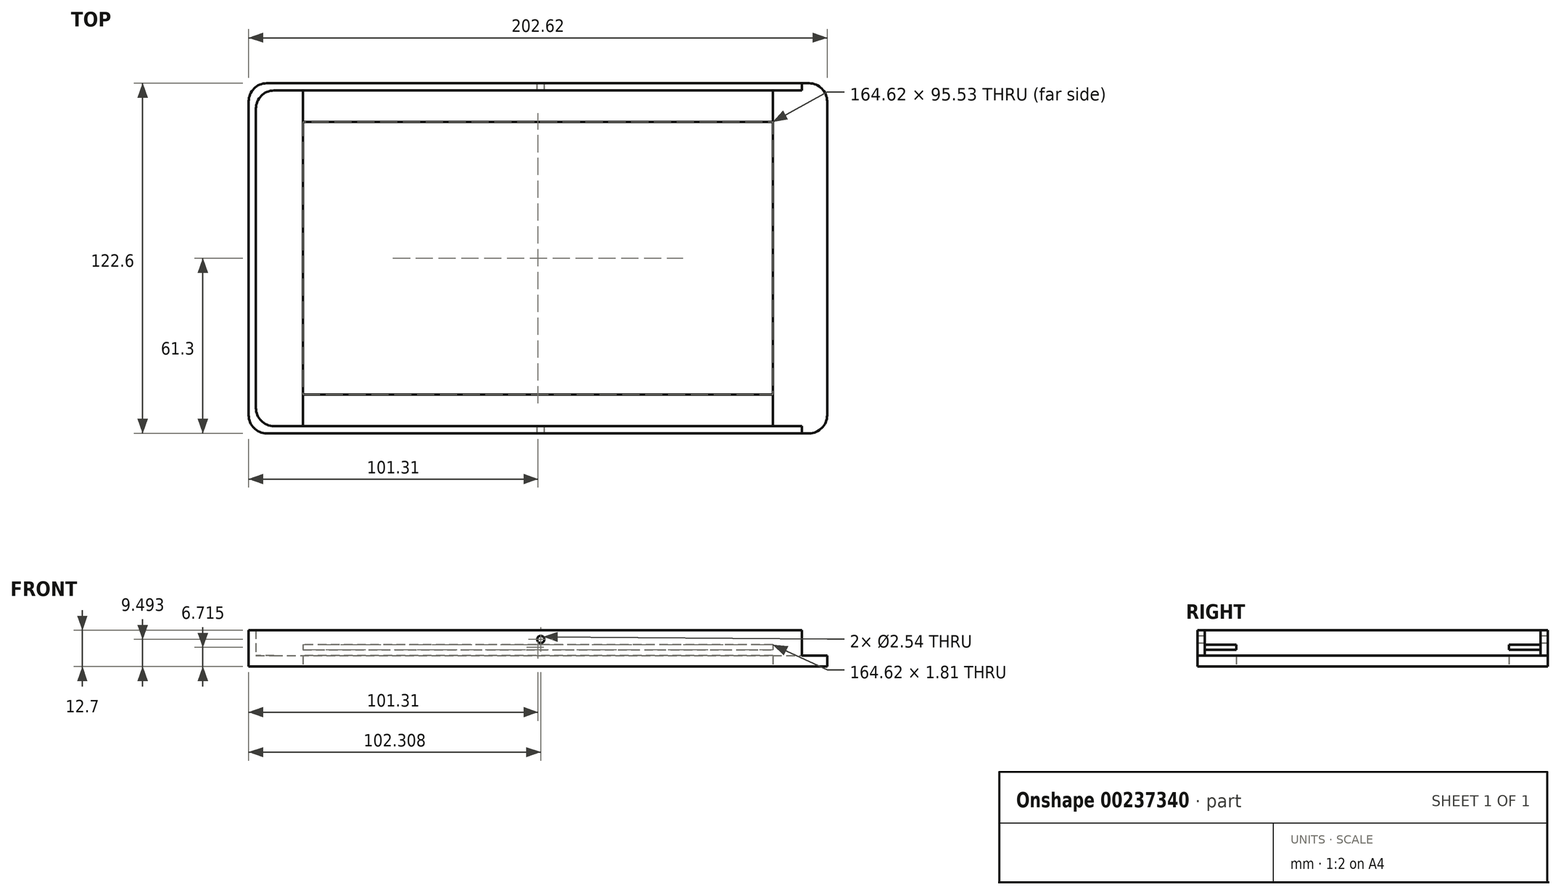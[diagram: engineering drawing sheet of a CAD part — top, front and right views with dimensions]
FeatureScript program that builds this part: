
annotation { "Feature Type Name" : "Feature", "Feature Type Description" : "" }
export const myFeature = defineFeature(function(context is Context, id is Id, definition is map)
    precondition{}
    {
        {
            var Q0;
            Q0=qCreatedBy(makeId("Top.planeOp"),FACE);
            var sketch = newSketch(context, id + "F0", { "sketchPlane" : qUnion([Q0])});
            skLineSegment(sketch, "E0.bottom", {"start": v(94.96, -61.3) * mm, "end": v(-94.96, -61.3) * mm});
            skLineSegment(sketch, "E0.top", {"start": v(94.96, 61.3) * mm, "end": v(-94.96, 61.3) * mm});
            skLineSegment(sketch, "E0.left", {"start": v(101.3, -54.95) * mm, "end": v(101.3, 54.95) * mm});
            skLineSegment(sketch, "E0.right", {"start": v(-101.3, -54.95) * mm, "end": v(-101.3, 54.95) * mm});
            skPoint(sketch, "E0.middle", {"position": v(0, 0) * mm});
            skPoint(sketch, "E1.visualSharp", {"position": v(101.3, -61.3) * mm});
            skArc(sketch, "E1.filletArc", {"start": v(94.96, -61.3) * mm, "mid": v(99.45, -59.44) * mm, "end": v(101.3, -54.95) * mm});
            skPoint(sketch, "E2.visualSharp", {"position": v(-101.3, -61.3) * mm});
            skArc(sketch, "E2.filletArc", {"start": v(-101.3, -54.95) * mm, "mid": v(-99.45, -59.44) * mm, "end": v(-94.96, -61.3) * mm});
            skPoint(sketch, "E3.visualSharp", {"position": v(-101.3, 61.3) * mm});
            skArc(sketch, "E3.filletArc", {"start": v(-94.96, 61.3) * mm, "mid": v(-99.45, 59.44) * mm, "end": v(-101.3, 54.95) * mm});
            skPoint(sketch, "E4.visualSharp", {"position": v(101.3, 61.3) * mm});
            skArc(sketch, "E4.filletArc", {"start": v(101.3, 54.95) * mm, "mid": v(99.45, 59.44) * mm, "end": v(94.96, 61.3) * mm});
            skLineSegment(sketch, "E5.0", {"start": v(-82.3, -54.95) * mm, "end": v(-82.3, 54.95) * mm});
            skLineSegment(sketch, "E6.0", {"start": v(82.3, -54.95) * mm, "end": v(-82.3, -54.95) * mm});
            skLineSegment(sketch, "E7.0", {"start": v(82.3, -54.95) * mm, "end": v(82.3, 54.95) * mm});
            skLineSegment(sketch, "E8.0", {"start": v(82.3, 54.95) * mm, "end": v(-82.3, 54.95) * mm});
            skSolve(sketch);
        }
        {
            var Q0;
            Q0=makeQuery(id+"F0.imprint","IMPRINT",FACE,{"disambiguationData":[TD([[makeQuery(id+"F0.imprint","IMPRINT",EDGE,{"derivedFrom":sQuery(id+"F0.wireOp",EDGE,"E0.bottom")}),-1.0]])]});
            extrude(context, id + "F1", {"entities" : qUnion([Q0]), "depth" : 3.8 * mm});
        }
        {
            var Q0;
            Q0=qCreatedBy(makeId("Top.planeOp"),FACE);
            var sketch = newSketch(context, id + "F2", { "sketchPlane" : qUnion([Q0])});
            skLineSegment(sketch, "E9.bottom", {"start": v(82.3, 58.76) * mm, "end": v(-82.3, 58.76) * mm});
            skLineSegment(sketch, "E9.top", {"start": v(82.3, 47.76) * mm, "end": v(-82.3, 47.76) * mm});
            skLineSegment(sketch, "E9.left", {"start": v(82.3, 58.76) * mm, "end": v(82.3, 47.76) * mm});
            skLineSegment(sketch, "E9.right", {"start": v(-82.3, 58.76) * mm, "end": v(-82.3, 47.76) * mm});
            skSolve(sketch);
        }
        {
            var Q0;
            Q0=makeQuery(id+"F2.imprint","IMPRINT",FACE,{"disambiguationData":[TD([[makeQuery(id+"F2.imprint","IMPRINT",EDGE,{"derivedFrom":sQuery(id+"F2.wireOp",EDGE,"E9.bottom")}),1.0]])]});
            extrude(context, id + "F3", {"entities" : qUnion([Q0]), "operationType" : NewBodyOperationType.ADD, "depth" : 7.62 * mm});
        }
        {
            var Q0;
            Q0=makeQuery(id+"F3.opExtrude","SWEPT_FACE",FACE,{"disambiguationData":[OSD([sQuery(id+"F2.wireOp",EDGE,"E9.top")])]});
            var sketch = newSketch(context, id + "F4", { "sketchPlane" : qUnion([Q0])});
            skLineSegment(sketch, "E10.bottom", {"start": v(-82.3, 5.81) * mm, "end": v(82.3, 5.81) * mm});
            skLineSegment(sketch, "E10.top", {"start": v(-82.3, 3.81) * mm, "end": v(82.3, 3.81) * mm});
            skLineSegment(sketch, "E10.left", {"start": v(-82.3, 5.81) * mm, "end": v(-82.3, 3.81) * mm});
            skLineSegment(sketch, "E10.right", {"start": v(82.3, 5.81) * mm, "end": v(82.3, 3.81) * mm});
            skSolve(sketch);
        }
        {
            var Q0;
            Q0=makeQuery(id+"F4.imprint","IMPRINT",FACE,{"disambiguationData":[TD([[makeQuery(id+"F4.imprint","IMPRINT",EDGE,{"derivedFrom":sQuery(id+"F4.wireOp",EDGE,"E10.bottom")}),-1.0]])]});
            extrude(context, id + "F5", {"entities" : qUnion([Q0]), "operationType" : NewBodyOperationType.REMOVE, "oppositeDirection" : true, "depth" : 11 * mm});
        }
        {
            var Q0;
            Q0=makeQuery(id+"F3.boolean.opBoolean","MERGE",FACE,{"derivedFrom":[makeQuery(id+"F1.opExtrude","CAP_FACE",FACE,{"disambiguationData":[OSD([sQuery(id+"F0.wireOp",EDGE,"E0.bottom"),sQuery(id+"F0.wireOp",EDGE,"E0.top"),sQuery(id+"F0.wireOp",EDGE,"E0.left"),sQuery(id+"F0.wireOp",EDGE,"E0.right"),sQuery(id+"F0.wireOp",EDGE,"E1.filletArc"),sQuery(id+"F0.wireOp",EDGE,"E2.filletArc"),sQuery(id+"F0.wireOp",EDGE,"E3.filletArc"),sQuery(id+"F0.wireOp",EDGE,"E4.filletArc"),sQuery(id+"F0.wireOp",EDGE,"E5.0"),sQuery(id+"F0.wireOp",EDGE,"E6.0"),sQuery(id+"F0.wireOp",EDGE,"E7.0"),sQuery(id+"F0.wireOp",EDGE,"E8.0")])],"isStart":true}),makeQuery(id+"F3.opExtrude","CAP_FACE",FACE,{"disambiguationData":[OSD([sQuery(id+"F2.wireOp",EDGE,"E9.bottom"),sQuery(id+"F2.wireOp",EDGE,"E9.top"),sQuery(id+"F2.wireOp",EDGE,"E9.left"),sQuery(id+"F2.wireOp",EDGE,"E9.right")])],"isStart":true})]});
            var sketch = newSketch(context, id + "F6", { "sketchPlane" : qUnion([Q0])});
            skLineSegment(sketch, "E11.bottom", {"start": v(82.3, 58.76) * mm, "end": v(-82.3, 58.76) * mm});
            skLineSegment(sketch, "E11.top", {"start": v(82.3, 47.76) * mm, "end": v(-82.3, 47.76) * mm});
            skLineSegment(sketch, "E11.left", {"start": v(82.3, 58.76) * mm, "end": v(82.3, 47.76) * mm});
            skLineSegment(sketch, "E11.right", {"start": v(-82.3, 58.76) * mm, "end": v(-82.3, 47.76) * mm});
            skSolve(sketch);
        }
        {
            var Q0;
            Q0 = qSketchRegion(id + "F6", true);
            extrude(context, id + "F7", {"entities" : qUnion([Q0]), "operationType" : NewBodyOperationType.ADD, "oppositeDirection" : true, "depth" : 7.62 * mm});
        }
        {
            var Q0;
            Q0=makeQuery(id+"F7.opExtrude","SWEPT_FACE",FACE,{"disambiguationData":[OSD([sQuery(id+"F6.wireOp",EDGE,"E11.top")])]});
            var sketch = newSketch(context, id + "F8", { "sketchPlane" : qUnion([Q0])});
            skLineSegment(sketch, "E12.bottom", {"start": v(-82.3, 5.81) * mm, "end": v(82.3, 5.81) * mm});
            skLineSegment(sketch, "E12.top", {"start": v(-82.3, 3.81) * mm, "end": v(82.3, 3.81) * mm});
            skLineSegment(sketch, "E12.left", {"start": v(-82.3, 5.81) * mm, "end": v(-82.3, 3.81) * mm});
            skLineSegment(sketch, "E12.right", {"start": v(82.3, 5.81) * mm, "end": v(82.3, 3.81) * mm});
            skSolve(sketch);
        }
        {
            var Q0;
            Q0=makeQuery(id+"F8.imprint","IMPRINT",FACE,{"disambiguationData":[TD([[makeQuery(id+"F8.imprint","IMPRINT",EDGE,{"derivedFrom":sQuery(id+"F8.wireOp",EDGE,"E12.bottom")}),-1.0]])]});
            extrude(context, id + "F9", {"entities" : qUnion([Q0]), "operationType" : NewBodyOperationType.REMOVE, "oppositeDirection" : true, "depth" : 11 * mm});
        }
        {
            var Q0;
            Q0=qCreatedBy(makeId("Top.planeOp"),FACE);
            var sketch = newSketch(context, id + "F10", { "sketchPlane" : qUnion([Q0])});
            skLineSegment(sketch, "E13.bottom", {"start": v(92.42, -61.3) * mm, "end": v(-94.96, -61.3) * mm});
            skLineSegment(sketch, "E13.top", {"start": v(94.96, 61.3) * mm, "end": v(-94.96, 61.3) * mm});
            skLineSegment(sketch, "E13.right", {"start": v(-101.3, -54.95) * mm, "end": v(-101.3, 54.95) * mm});
            skPoint(sketch, "E13.middle", {"position": v(0, 0) * mm});
            skPoint(sketch, "E14.visualSharp", {"position": v(101.3, -61.3) * mm});
            skArc(sketch, "E14.filletArc", {"start": v(92.42, -61.3) * mm, "mid": v(96.9, -59.44) * mm, "end": v(98.77, -54.95) * mm});
            skPoint(sketch, "E15.visualSharp", {"position": v(-101.3, -61.3) * mm});
            skArc(sketch, "E15.filletArc", {"start": v(-101.3, -54.95) * mm, "mid": v(-99.45, -59.44) * mm, "end": v(-94.96, -61.3) * mm});
            skPoint(sketch, "E16.visualSharp", {"position": v(-101.3, 61.3) * mm});
            skArc(sketch, "E16.filletArc", {"start": v(-94.96, 61.3) * mm, "mid": v(-99.45, 59.44) * mm, "end": v(-101.3, 54.95) * mm});
            skPoint(sketch, "E17.visualSharp", {"position": v(101.3, 61.3) * mm});
            skArc(sketch, "E17.filletArc", {"start": v(101.3, 54.95) * mm, "mid": v(99.45, 59.44) * mm, "end": v(94.96, 61.3) * mm});
            skLineSegment(sketch, "E18.0", {"start": v(-98.77, -50.97) * mm, "end": v(-98.77, 52.42) * mm});
            skLineSegment(sketch, "E19.0", {"start": v(92.42, -58.76) * mm, "end": v(-92.42, -58.76) * mm});
            skLineSegment(sketch, "E20.0", {"start": v(94.96, 58.76) * mm, "end": v(-92.42, 58.76) * mm});
            skLineSegment(sketch, "E21", {"start": v(94.96, 58.76) * mm, "end": v(101.3, 54.95) * mm});
            skLineSegment(sketch, "E22", {"start": v(98.77, -54.95) * mm, "end": v(92.42, -58.76) * mm});
            skPoint(sketch, "E23", {"position": v(-94.96, -58.76) * mm});
            skPoint(sketch, "E24", {"position": v(-98.77, -54.95) * mm});
            skLineSegment(sketch, "E25", {"start": v(-98.77, -50.97) * mm, "end": v(-98.77, -52.41) * mm});
            skPoint(sketch, "E26", {"position": v(-92.42, 58.76) * mm});
            skPoint(sketch, "E27", {"position": v(-98.77, 52.41) * mm});
            skPoint(sketch, "E28", {"position": v(-92.42, 52.41) * mm});
            skArc(sketch, "E29", {"start": v(-92.42, 58.76) * mm, "mid": v(-96.9, 56.9) * mm, "end": v(-98.77, 52.41) * mm});
            skPoint(sketch, "E30.orphan", {"position": v(-94.96, 58.76) * mm});
            skPoint(sketch, "E31.orphan", {"position": v(-98.77, 54.95) * mm});
            skPoint(sketch, "E32", {"position": v(-92.42, -52.41) * mm});
            skPoint(sketch, "E33.orphan", {"position": v(-92.42, -61.3) * mm});
            skArc(sketch, "E34", {"start": v(-98.77, -52.41) * mm, "mid": v(-96.9, -56.9) * mm, "end": v(-92.42, -58.76) * mm});
            skSolve(sketch);
        }
        {
            var Q0;
            Q0 = qSketchRegion(id + "F10", true);
            extrude(context, id + "F11", {"entities" : qUnion([Q0]), "operationType" : NewBodyOperationType.ADD, "depth" : 12.7 * mm});
        }
        {
            var Q0;
            Q0=makeQuery(id+"F11.boolean.opBoolean","MERGE",FACE,{"derivedFrom":[makeQuery(id+"F1.opExtrude","SWEPT_FACE",FACE,{"disambiguationData":[OSD([sQuery(id+"F0.wireOp",EDGE,"E0.bottom")])]}),makeQuery(id+"F11.opExtrude","SWEPT_FACE",FACE,{"disambiguationData":[OSD([sQuery(id+"F10.wireOp",EDGE,"E13.bottom")])]})]});
            var sketch = newSketch(context, id + "F12", { "sketchPlane" : qUnion([Q0])});
            skLineSegment(sketch, "E35.bottom", {"start": v(92.42, 12.7) * mm, "end": v(106.23, 12.7) * mm});
            skLineSegment(sketch, "E35.top", {"start": v(92.42, 3.81) * mm, "end": v(106.23, 3.81) * mm});
            skLineSegment(sketch, "E35.left", {"start": v(92.42, 12.7) * mm, "end": v(92.42, 3.81) * mm});
            skLineSegment(sketch, "E35.right", {"start": v(106.23, 12.7) * mm, "end": v(106.23, 3.81) * mm});
            skSolve(sketch);
        }
        {
            var Q0;
            Q0=makeQuery(id+"F12.imprint","IMPRINT",FACE,{"disambiguationData":[TD([[makeQuery(id+"F12.imprint","IMPRINT",EDGE,{"derivedFrom":sQuery(id+"F12.wireOp",EDGE,"E35.bottom")}),-1.0]])]});
            extrude(context, id + "F13", {"entities" : qUnion([Q0]), "operationType" : NewBodyOperationType.REMOVE, "oppositeDirection" : true, "depth" : 127 * mm});
        }
        {
            var Q0;
            Q0=makeQuery(id+"F11.boolean.opBoolean","MERGE",FACE,{"derivedFrom":[makeQuery(id+"F1.opExtrude","SWEPT_FACE",FACE,{"disambiguationData":[OSD([sQuery(id+"F0.wireOp",EDGE,"E0.top")])]}),makeQuery(id+"F11.opExtrude","SWEPT_FACE",FACE,{"disambiguationData":[OSD([sQuery(id+"F10.wireOp",EDGE,"E13.top")])]})]});
            var sketch = newSketch(context, id + "F14", { "sketchPlane" : qUnion([Q0])});
            skPoint(sketch, "E36", {"position": v(0, 6.35) * mm});
            skPoint(sketch, "E36.positionSnap0", {"position": v(94.96, 6.35) * mm});
            skPoint(sketch, "E37", {"position": v(0, 9.5) * mm});
            skPoint(sketch, "E38", {"position": v(-1, 9.5) * mm});
            skSolve(sketch);
        }
        {
            var Q0;
            Q0=sQuery(id+"F14.wireOp",VERTEX,"E38");
            var Q1;
            Q1=makeQuery(id+"F5.boolean.opBoolean","SPLIT",BODY,{"disambiguationData":[OD(1.0)],"derivedFrom":makeQuery(id+"F1.opExtrude","SWEPT_BODY",BODY,{"disambiguationData":[OSD([sQuery(id+"F0.wireOp",EDGE,"E0.bottom"),sQuery(id+"F0.wireOp",EDGE,"E0.top"),sQuery(id+"F0.wireOp",EDGE,"E0.left"),sQuery(id+"F0.wireOp",EDGE,"E0.right"),sQuery(id+"F0.wireOp",EDGE,"E1.filletArc"),sQuery(id+"F0.wireOp",EDGE,"E2.filletArc"),sQuery(id+"F0.wireOp",EDGE,"E3.filletArc"),sQuery(id+"F0.wireOp",EDGE,"E4.filletArc"),sQuery(id+"F0.wireOp",EDGE,"E5.0"),sQuery(id+"F0.wireOp",EDGE,"E6.0"),sQuery(id+"F0.wireOp",EDGE,"E7.0"),sQuery(id+"F0.wireOp",EDGE,"E8.0")])]})});
            hole(context, id + "F15", {"style" : HoleStyle.SIMPLE, "endStyle" : HoleEndStyle.THROUGH, "holeDiameter" : 2.54 * mm, "tappedDepth" : 12.7 * mm, "tapClearance" : 3, "startFromSketch" : true, "locations" : qUnion([Q0]), "scope" : qUnion([Q1])});
        }
    });
